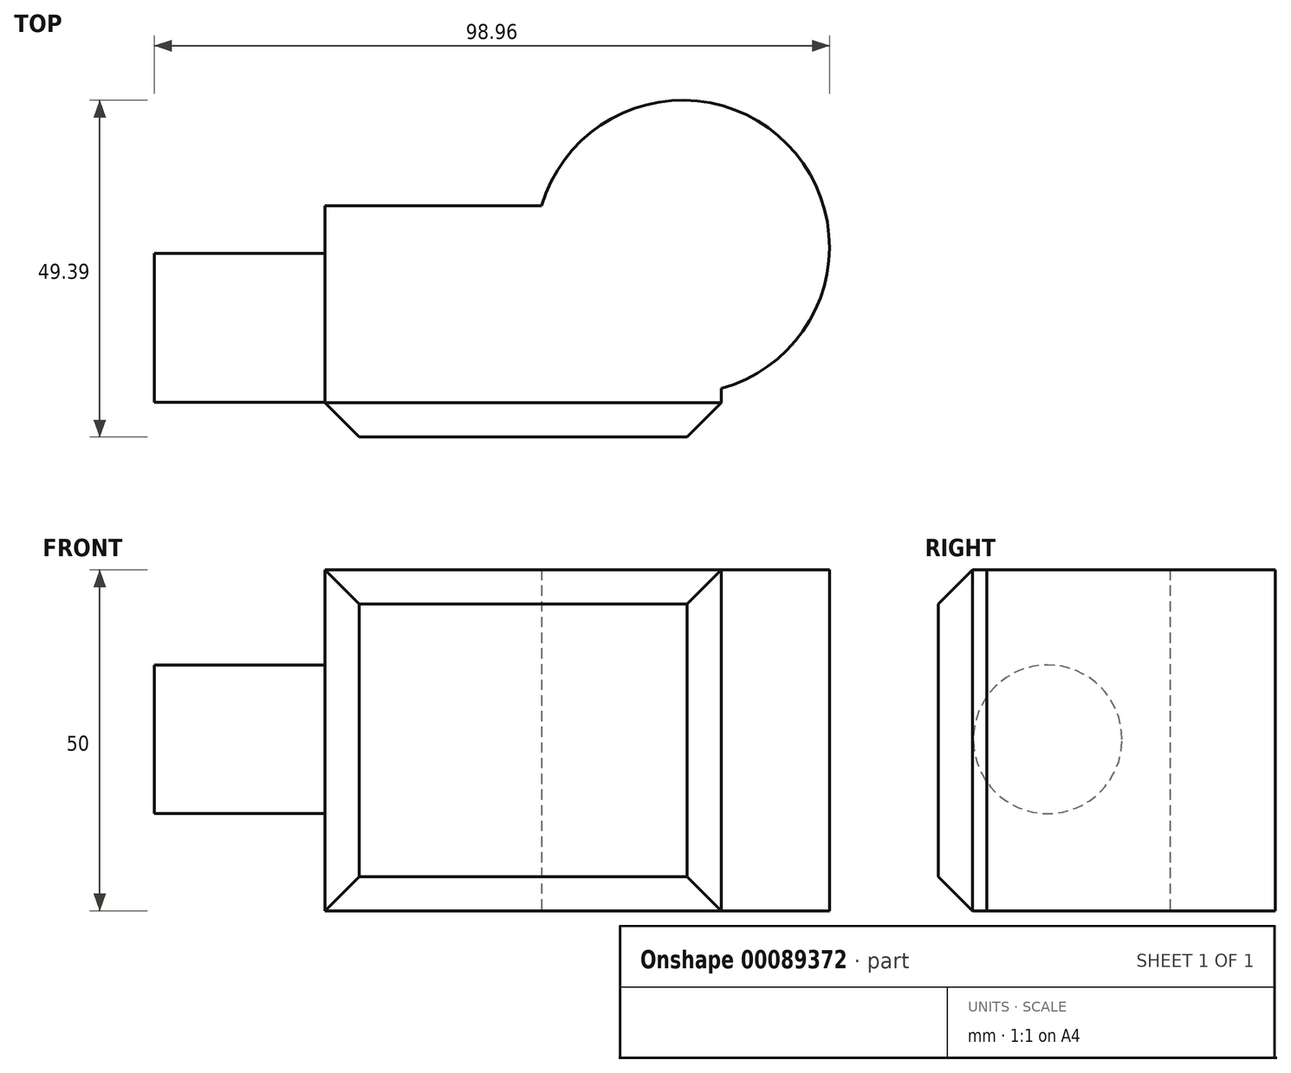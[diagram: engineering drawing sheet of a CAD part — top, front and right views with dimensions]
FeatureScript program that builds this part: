
annotation { "Feature Type Name" : "Feature", "Feature Type Description" : "" }
export const myFeature = defineFeature(function(context is Context, id is Id, definition is map)
    precondition{}
    {
        {
            var Q0;
            Q0=qCreatedBy(makeId("Top.planeOp"),FACE);
            var sketch = newSketch(context, id + "F0", { "sketchPlane" : qUnion([Q0])});
            skLineSegment(sketch, "E0.bottom", {"start": v(-35.02, -24.84) * mm, "end": v(23.1, -24.84) * mm});
            skLineSegment(sketch, "E0.top", {"start": v(-35.02, 9.08) * mm, "end": v(23.1, 9.08) * mm});
            skLineSegment(sketch, "E0.left", {"start": v(-35.02, -24.84) * mm, "end": v(-35.02, 9.08) * mm});
            skLineSegment(sketch, "E0.right", {"start": v(23.1, -24.84) * mm, "end": v(23.1, 9.08) * mm});
            skCircle(sketch, "E1", {"center": v(17.42, 3.03) * mm, "radius": 21.52 * mm});
            skSolve(sketch);
        }
        {
            var Q0;
            {var subQ1=sQuery(id+"F0.wireOp",EDGE,"E0.bottom");Q0=makeQuery(id+"F0.imprint","IMPRINT",FACE,{"disambiguationData":[TD([[makeQuery(id+"F0.imprint","IMPRINT",EDGE,{"derivedFrom":subQ1}),1.0]])]});}
            var Q1;
            {var subQ0=sQuery(id+"F0.wireOp",EDGE,"E0.right");var subQ1=sQuery(id+"F0.wireOp",EDGE,"E0.top");var subQ2=makeQuery(id+"F0.imprint","INTERSECT",VERTEX,{"derivedFrom":[subQ1,subQ0]});Q1=makeQuery(id+"F0.imprint","IMPRINT",FACE,{"disambiguationData":[TD([[makeQuery(id+"F0.imprint","IMPRINT",EDGE,{"disambiguationData":[TD([[subQ2,1.0]])],"derivedFrom":subQ1}),1.0]])]});}
            var Q2;
            {var subQ0=sQuery(id+"F0.wireOp",EDGE,"E0.right");var subQ1=sQuery(id+"F0.wireOp",EDGE,"E0.top");var subQ2=makeQuery(id+"F0.imprint","INTERSECT",VERTEX,{"derivedFrom":[subQ1,subQ0]});Q2=makeQuery(id+"F0.imprint","IMPRINT",FACE,{"disambiguationData":[TD([[makeQuery(id+"F0.imprint","IMPRINT",EDGE,{"disambiguationData":[TD([[subQ2,1.0]])],"derivedFrom":subQ1}),-1.0]])]});}
            extrude(context, id + "F1", {"entities" : qUnion([Q0, Q1, Q2]), "depth" : 50 * mm});
        }
        {
            var Q0;
            Q0=makeQuery(id+"F1.opExtrude","SWEPT_FACE",FACE,{"disambiguationData":[OSD([sQuery(id+"F0.wireOp",EDGE,"E0.left")])]});
            var sketch = newSketch(context, id + "F2", { "sketchPlane" : qUnion([Q0])});
            skCircle(sketch, "E2", {"center": v(8.84, 25.15) * mm, "radius": 10.9 * mm});
            skSolve(sketch);
        }
        {
            var Q0;
            Q0 = qSketchRegion(id + "F2", true);
            extrude(context, id + "F3", {"entities" : qUnion([Q0]), "operationType" : NewBodyOperationType.ADD, "depth" : 25 * mm});
        }
        {
            var Q0;
            Q0=makeQuery(id+"F1.opExtrude","SWEPT_EDGE",EDGE,{"disambiguationData":[OSD([sQuery(id+"F0.wireOp",EDGE,"E0.bottom"),sQuery(id+"F0.wireOp",EDGE,"E0.right")])]});
            var Q1;
            Q1=makeQuery(id+"F1.opExtrude","SWEPT_FACE",FACE,{"disambiguationData":[OSD([sQuery(id+"F0.wireOp",EDGE,"E0.bottom")])]});
            chamfer(context, id + "F4", {"entities" : qUnion([Q0, Q1]), "width" : 5 * mm, "tangentPropagation" : true});
        }
    });
